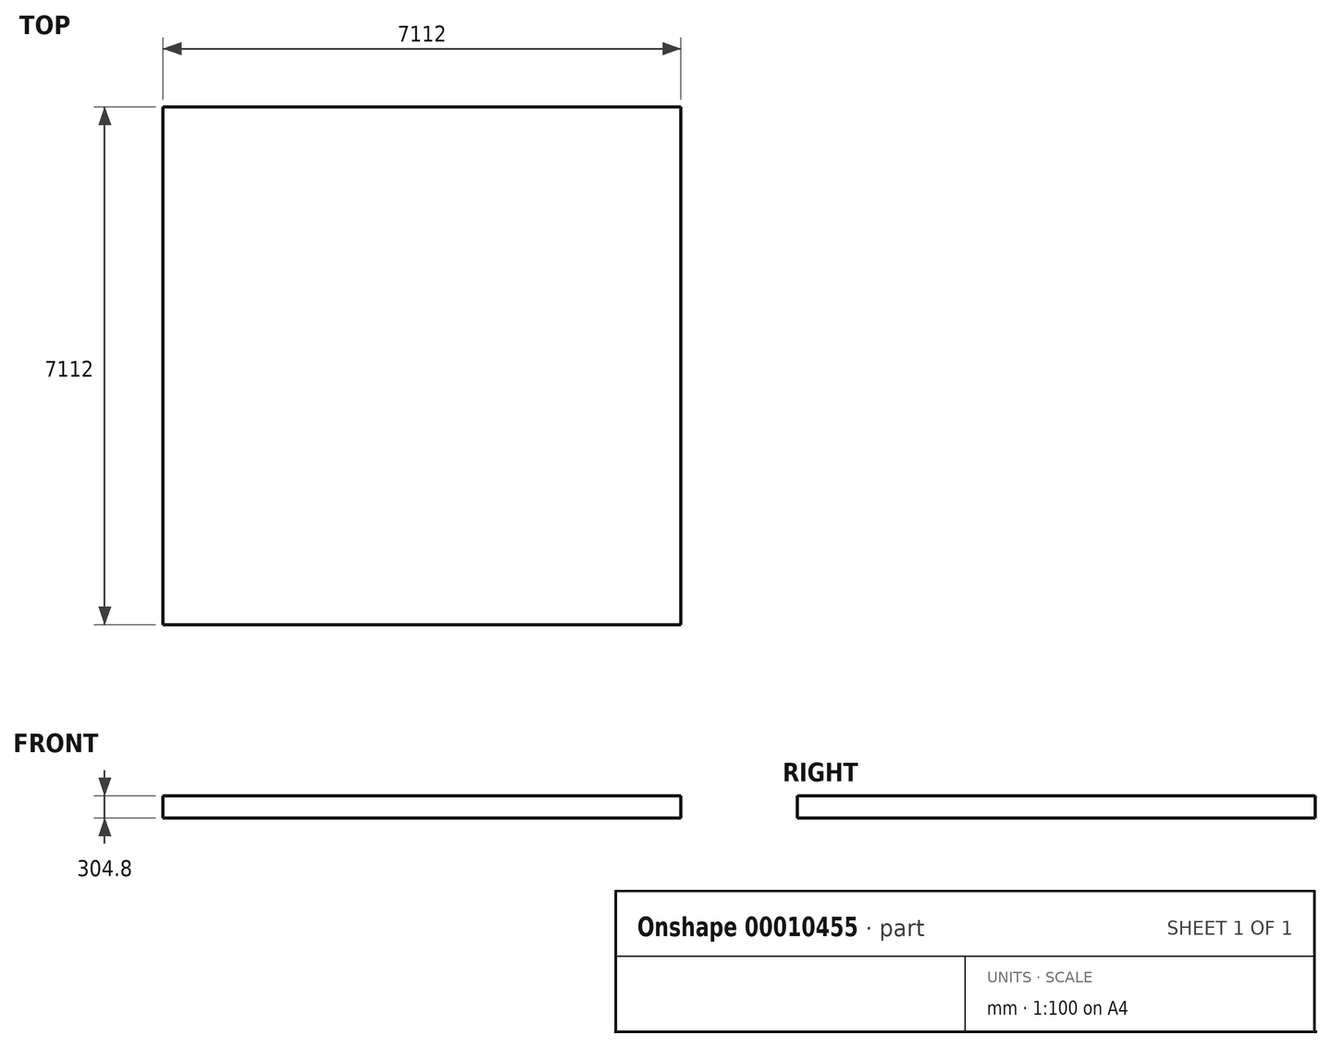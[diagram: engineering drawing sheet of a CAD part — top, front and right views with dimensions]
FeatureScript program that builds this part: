
annotation { "Feature Type Name" : "Feature", "Feature Type Description" : "" }
export const myFeature = defineFeature(function(context is Context, id is Id, definition is map)
    precondition{}
    {
        {
            var Q0;
            Q0=qCreatedBy(makeId("Top.planeOp"),FACE);
            var sketch = newSketch(context, id + "F0", { "sketchPlane" : qUnion([Q0])});
            skLineSegment(sketch, "E0.bottom", {"start": v(0, 7112) * mm, "end": v(7112, 7112) * mm});
            skLineSegment(sketch, "E0.top", {"start": v(0, 0) * mm, "end": v(7112, 0) * mm});
            skLineSegment(sketch, "E0.left", {"start": v(0, 7112) * mm, "end": v(0, 0) * mm});
            skLineSegment(sketch, "E0.right", {"start": v(7112, 7112) * mm, "end": v(7112, 0) * mm});
            skSolve(sketch);
        }
        {
            var Q0;
            Q0=makeQuery(id+"F0.imprint","IMPRINT",FACE,{"disambiguationData":[TD([[makeQuery(id+"F0.imprint","IMPRINT",EDGE,{"derivedFrom":sQuery(id+"F0.wireOp",EDGE,"E0.bottom")}),-1.0]])]});
            var Q1;
            Q1=sQuery(id+"F0.wireOp",EDGE,"E0.left");
            extrude(context, id + "F1", {"entities" : qUnion([Q0]), "surfaceEntities" : qUnion([Q1]), "depth" : 304.8 * mm});
        }
    });
